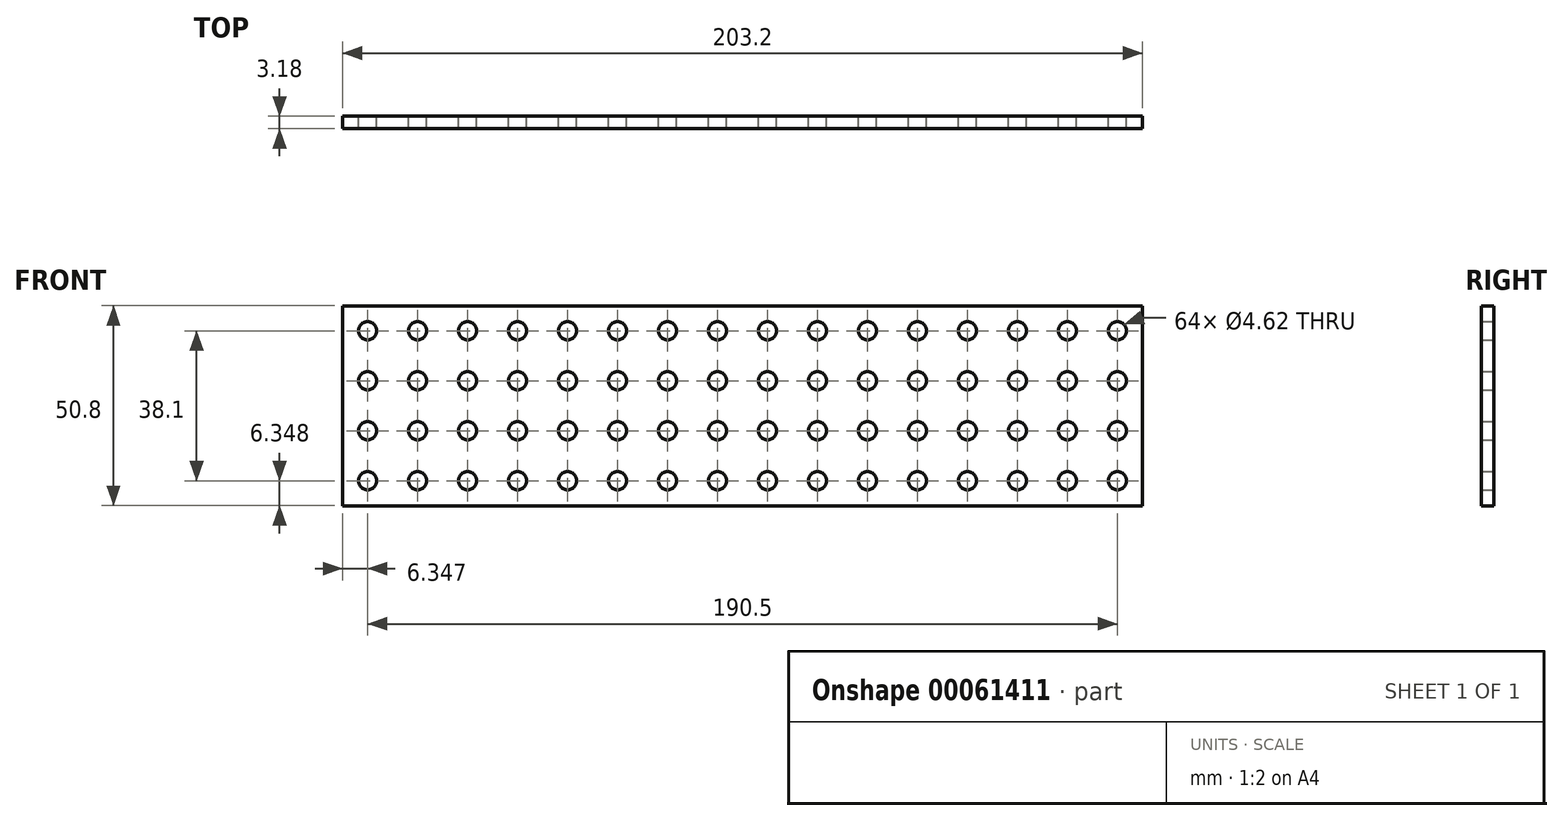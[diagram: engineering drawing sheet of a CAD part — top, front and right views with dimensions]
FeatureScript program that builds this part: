
annotation { "Feature Type Name" : "Feature", "Feature Type Description" : "" }
export const myFeature = defineFeature(function(context is Context, id is Id, definition is map)
    precondition{}
    {
        {
            var Q0;
            Q0=qCreatedBy(makeId("Front.planeOp"),FACE);
            var sketch = newSketch(context, id + "F0", { "sketchPlane" : qUnion([Q0])});
            skLineSegment(sketch, "E0.bottom", {"start": v(-82.78, 25.83) * mm, "end": v(120.42, 25.83) * mm});
            skLineSegment(sketch, "E0.top", {"start": v(-82.78, -24.97) * mm, "end": v(120.42, -24.97) * mm});
            skLineSegment(sketch, "E0.left", {"start": v(-82.78, 25.83) * mm, "end": v(-82.78, -24.97) * mm});
            skLineSegment(sketch, "E0.right", {"start": v(120.42, 25.83) * mm, "end": v(120.42, -24.97) * mm});
            skLineSegment(sketch, "E1", {"start": v(-82.78, 19.48) * mm, "end": v(-82.78, 25.83) * mm, "construction": true});
            skLineSegment(sketch, "E2", {"start": v(-82.78, 25.83) * mm, "end": v(-76.43, 25.83) * mm, "construction": true});
            skCircle(sketch, "E3", {"center": v(-76.43, 19.48) * mm, "radius": 2.31 * mm});
            skCircle(sketch, "E4.0.1.0", {"center": v(-76.43, 6.78) * mm, "radius": 2.31 * mm});
            skCircle(sketch, "E4.0.2.0", {"center": v(-76.43, -5.92) * mm, "radius": 2.31 * mm});
            skCircle(sketch, "E4.0.3.0", {"center": v(-76.43, -18.62) * mm, "radius": 2.31 * mm});
            skCircle(sketch, "E4.1.0.0", {"center": v(-63.73, 19.48) * mm, "radius": 2.31 * mm});
            skCircle(sketch, "E4.1.1.0", {"center": v(-63.73, 6.78) * mm, "radius": 2.31 * mm});
            skCircle(sketch, "E4.1.2.0", {"center": v(-63.73, -5.92) * mm, "radius": 2.31 * mm});
            skCircle(sketch, "E4.1.3.0", {"center": v(-63.73, -18.62) * mm, "radius": 2.31 * mm});
            skCircle(sketch, "E4.2.0.0", {"center": v(-51.03, 19.48) * mm, "radius": 2.31 * mm});
            skCircle(sketch, "E4.2.1.0", {"center": v(-51.03, 6.78) * mm, "radius": 2.31 * mm});
            skCircle(sketch, "E4.2.2.0", {"center": v(-51.03, -5.92) * mm, "radius": 2.31 * mm});
            skCircle(sketch, "E4.2.3.0", {"center": v(-51.03, -18.62) * mm, "radius": 2.31 * mm});
            skCircle(sketch, "E4.3.0.0", {"center": v(-38.33, 19.48) * mm, "radius": 2.31 * mm});
            skCircle(sketch, "E4.3.1.0", {"center": v(-38.33, 6.78) * mm, "radius": 2.31 * mm});
            skCircle(sketch, "E4.3.2.0", {"center": v(-38.33, -5.92) * mm, "radius": 2.31 * mm});
            skCircle(sketch, "E4.3.3.0", {"center": v(-38.33, -18.62) * mm, "radius": 2.31 * mm});
            skCircle(sketch, "E4.4.0.0", {"center": v(-25.63, 19.48) * mm, "radius": 2.31 * mm});
            skCircle(sketch, "E4.4.1.0", {"center": v(-25.63, 6.78) * mm, "radius": 2.31 * mm});
            skCircle(sketch, "E4.4.2.0", {"center": v(-25.63, -5.92) * mm, "radius": 2.31 * mm});
            skCircle(sketch, "E4.4.3.0", {"center": v(-25.63, -18.62) * mm, "radius": 2.31 * mm});
            skCircle(sketch, "E4.5.0.0", {"center": v(-12.93, 19.48) * mm, "radius": 2.31 * mm});
            skCircle(sketch, "E4.5.1.0", {"center": v(-12.93, 6.78) * mm, "radius": 2.31 * mm});
            skCircle(sketch, "E4.5.2.0", {"center": v(-12.93, -5.92) * mm, "radius": 2.31 * mm});
            skCircle(sketch, "E4.5.3.0", {"center": v(-12.93, -18.62) * mm, "radius": 2.31 * mm});
            skCircle(sketch, "E4.6.0.0", {"center": v(-0.23, 19.48) * mm, "radius": 2.31 * mm});
            skCircle(sketch, "E4.6.1.0", {"center": v(-0.23, 6.78) * mm, "radius": 2.31 * mm});
            skCircle(sketch, "E4.6.2.0", {"center": v(-0.23, -5.92) * mm, "radius": 2.31 * mm});
            skCircle(sketch, "E4.6.3.0", {"center": v(-0.23, -18.62) * mm, "radius": 2.31 * mm});
            skCircle(sketch, "E4.7.0.0", {"center": v(12.47, 19.48) * mm, "radius": 2.31 * mm});
            skCircle(sketch, "E4.7.1.0", {"center": v(12.47, 6.78) * mm, "radius": 2.31 * mm});
            skCircle(sketch, "E4.7.2.0", {"center": v(12.47, -5.92) * mm, "radius": 2.31 * mm});
            skCircle(sketch, "E4.7.3.0", {"center": v(12.47, -18.62) * mm, "radius": 2.31 * mm});
            skCircle(sketch, "E4.8.0.0", {"center": v(25.17, 19.48) * mm, "radius": 2.31 * mm});
            skCircle(sketch, "E4.8.1.0", {"center": v(25.17, 6.78) * mm, "radius": 2.31 * mm});
            skCircle(sketch, "E4.8.2.0", {"center": v(25.17, -5.92) * mm, "radius": 2.31 * mm});
            skCircle(sketch, "E4.8.3.0", {"center": v(25.17, -18.62) * mm, "radius": 2.31 * mm});
            skCircle(sketch, "E4.9.0.0", {"center": v(37.87, 19.48) * mm, "radius": 2.31 * mm});
            skCircle(sketch, "E4.9.1.0", {"center": v(37.87, 6.78) * mm, "radius": 2.31 * mm});
            skCircle(sketch, "E4.9.2.0", {"center": v(37.87, -5.92) * mm, "radius": 2.31 * mm});
            skCircle(sketch, "E4.9.3.0", {"center": v(37.87, -18.62) * mm, "radius": 2.31 * mm});
            skCircle(sketch, "E4.10.0.0", {"center": v(50.57, 19.48) * mm, "radius": 2.31 * mm});
            skCircle(sketch, "E4.10.1.0", {"center": v(50.57, 6.78) * mm, "radius": 2.31 * mm});
            skCircle(sketch, "E4.10.2.0", {"center": v(50.57, -5.92) * mm, "radius": 2.31 * mm});
            skCircle(sketch, "E4.10.3.0", {"center": v(50.57, -18.62) * mm, "radius": 2.31 * mm});
            skCircle(sketch, "E4.11.0.0", {"center": v(63.27, 19.48) * mm, "radius": 2.31 * mm});
            skCircle(sketch, "E4.11.1.0", {"center": v(63.27, 6.78) * mm, "radius": 2.31 * mm});
            skCircle(sketch, "E4.11.2.0", {"center": v(63.27, -5.92) * mm, "radius": 2.31 * mm});
            skCircle(sketch, "E4.11.3.0", {"center": v(63.27, -18.62) * mm, "radius": 2.31 * mm});
            skCircle(sketch, "E4.12.0.0", {"center": v(75.97, 19.48) * mm, "radius": 2.31 * mm});
            skCircle(sketch, "E4.12.1.0", {"center": v(75.97, 6.78) * mm, "radius": 2.31 * mm});
            skCircle(sketch, "E4.12.2.0", {"center": v(75.97, -5.92) * mm, "radius": 2.31 * mm});
            skCircle(sketch, "E4.12.3.0", {"center": v(75.97, -18.62) * mm, "radius": 2.31 * mm});
            skCircle(sketch, "E4.13.0.0", {"center": v(88.67, 19.48) * mm, "radius": 2.31 * mm});
            skCircle(sketch, "E4.13.1.0", {"center": v(88.67, 6.78) * mm, "radius": 2.31 * mm});
            skCircle(sketch, "E4.13.2.0", {"center": v(88.67, -5.92) * mm, "radius": 2.31 * mm});
            skCircle(sketch, "E4.13.3.0", {"center": v(88.67, -18.62) * mm, "radius": 2.31 * mm});
            skCircle(sketch, "E4.14.0.0", {"center": v(101.37, 19.48) * mm, "radius": 2.31 * mm});
            skCircle(sketch, "E4.14.1.0", {"center": v(101.37, 6.78) * mm, "radius": 2.31 * mm});
            skCircle(sketch, "E4.14.2.0", {"center": v(101.37, -5.92) * mm, "radius": 2.31 * mm});
            skCircle(sketch, "E4.14.3.0", {"center": v(101.37, -18.62) * mm, "radius": 2.31 * mm});
            skCircle(sketch, "E4.15.0.0", {"center": v(114.07, 19.48) * mm, "radius": 2.31 * mm});
            skCircle(sketch, "E4.15.1.0", {"center": v(114.07, 6.78) * mm, "radius": 2.31 * mm});
            skCircle(sketch, "E4.15.2.0", {"center": v(114.07, -5.92) * mm, "radius": 2.31 * mm});
            skCircle(sketch, "E4.15.3.0", {"center": v(114.07, -18.62) * mm, "radius": 2.31 * mm});
            skSolve(sketch);
        }
        {
            var Q0;
            Q0=makeQuery(id+"F0.imprint","IMPRINT",FACE,{"disambiguationData":[TD([[makeQuery(id+"F0.imprint","IMPRINT",EDGE,{"derivedFrom":sQuery(id+"F0.wireOp",EDGE,"E0.bottom")}),-1.0]])]});
            extrude(context, id + "F1", {"entities" : qUnion([Q0]), "depth" : 3.17 * mm});
        }
    });
